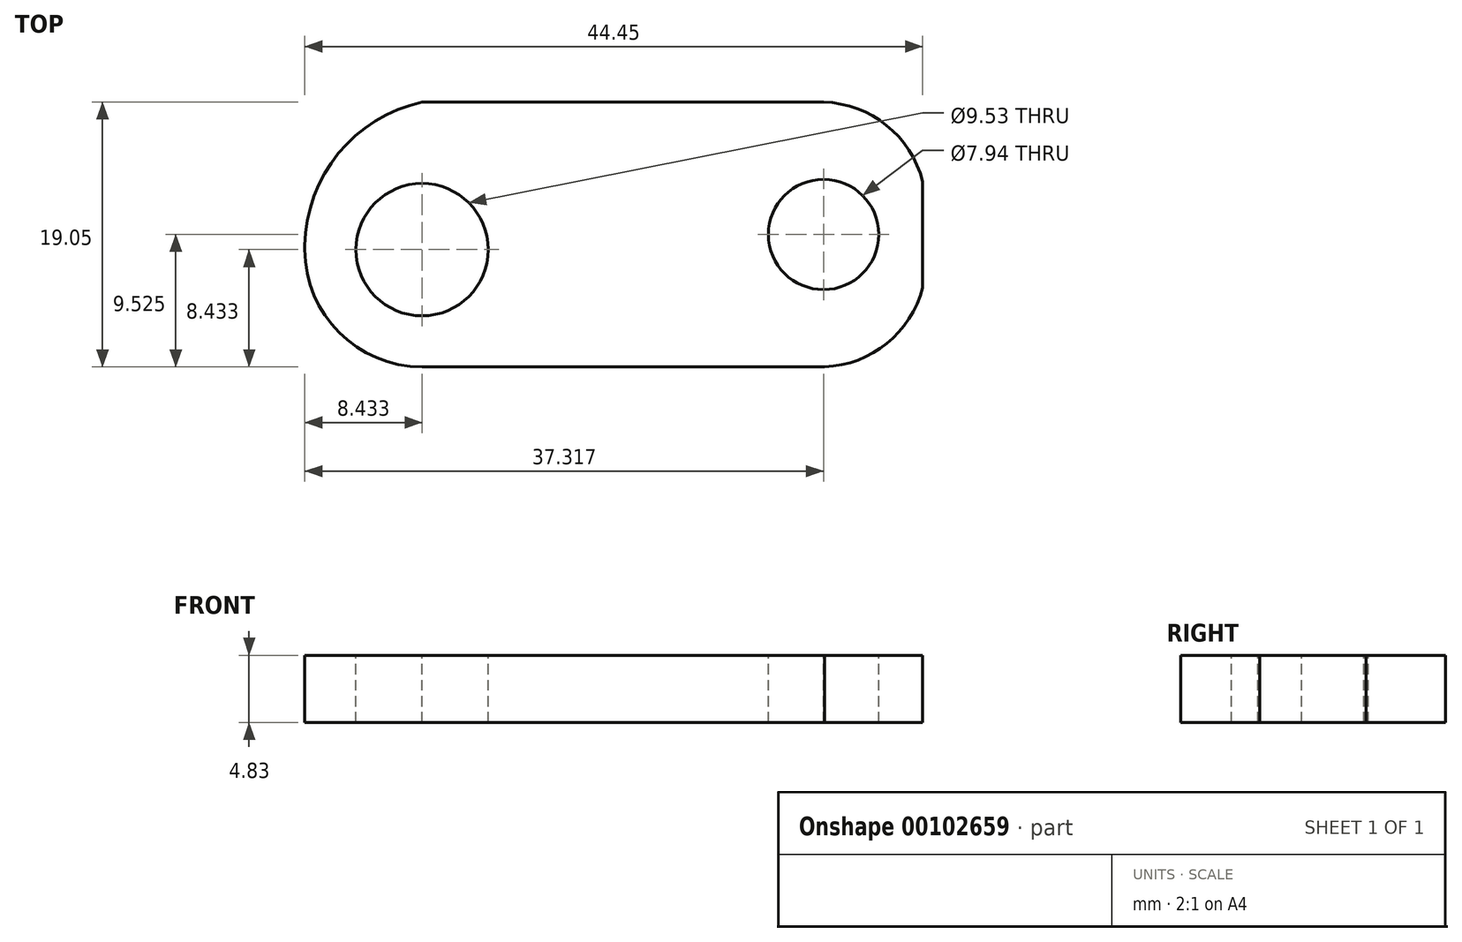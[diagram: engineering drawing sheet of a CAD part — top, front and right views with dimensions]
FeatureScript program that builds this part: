
annotation { "Feature Type Name" : "Feature", "Feature Type Description" : "" }
export const myFeature = defineFeature(function(context is Context, id is Id, definition is map)
    precondition{}
    {
        {
            var Q0;
            Q0=qCreatedBy(makeId("Top.planeOp"),FACE);
            var sketch = newSketch(context, id + "F0", { "sketchPlane" : qUnion([Q0])});
            skLineSegment(sketch, "E0.bottom", {"start": v(0, 0) * mm, "end": v(44.45, 0) * mm});
            skLineSegment(sketch, "E0.top", {"start": v(0, 19.05) * mm, "end": v(44.45, 19.05) * mm});
            skLineSegment(sketch, "E0.left", {"start": v(0, 0) * mm, "end": v(0, 19.05) * mm});
            skLineSegment(sketch, "E0.right", {"start": v(44.45, 0) * mm, "end": v(44.45, 19.05) * mm});
            skSolve(sketch);
        }
        {
            var Q0;
            Q0 = qSketchRegion(id + "F0", true);
            extrude(context, id + "F1", {"entities" : qUnion([Q0]), "depth" : 4.83 * mm});
        }
        {
            var Q0;
            Q0=makeQuery(id+"F1.opExtrude","CAP_FACE",FACE,{"disambiguationData":[OSD([sQuery(id+"F0.wireOp",EDGE,"E0.bottom"),sQuery(id+"F0.wireOp",EDGE,"E0.top"),sQuery(id+"F0.wireOp",EDGE,"E0.left"),sQuery(id+"F0.wireOp",EDGE,"E0.right")])],"isStart":false});
            var sketch = newSketch(context, id + "F2", { "sketchPlane" : qUnion([Q0])});
            skCircle(sketch, "E1", {"center": v(8.43, 8.43) * mm, "radius": 4.76 * mm});
            skCircle(sketch, "E2", {"center": v(37.32, 9.52) * mm, "radius": 3.97 * mm});
            skPoint(sketch, "E2.centerSnap0", {"position": v(44.45, 9.53) * mm});
            skArc(sketch, "E3", {"start": v(44.45, 13.34) * mm, "mid": v(41.83, 17.38) * mm, "end": v(37.32, 19.05) * mm});
            skArc(sketch, "E4", {"start": v(37.4, 0) * mm, "mid": v(41.86, 1.69) * mm, "end": v(44.45, 5.7) * mm});
            skLineSegment(sketch, "E5.0", {"start": v(44.45, 5.7) * mm, "end": v(44.45, 13.34) * mm});
            skPoint(sketch, "E6.orphan", {"position": v(44.45, 0) * mm});
            skPoint(sketch, "E7.orphan", {"position": v(44.45, 19.05) * mm});
            skArc(sketch, "E8", {"start": v(8.43, 19.05) * mm, "mid": v(2.32, 15.24) * mm, "end": v(0, 8.43) * mm});
            skLineSegment(sketch, "E9", {"start": v(0, 8.43) * mm, "end": v(0, 8.43) * mm});
            skArc(sketch, "E10", {"start": v(0, 8.43) * mm, "mid": v(2.55, 2.4) * mm, "end": v(8.66, 0) * mm});
            skSolve(sketch);
        }
        {
            var Q0;
            Q0 = qSketchRegion(id + "F2", true);
            var Q1;
            {var subQ0=sQuery(id+"F2.wireOp",EDGE,"E8");var subQ1=makeQuery(id+"F1.opExtrude","CAP_EDGE",EDGE,{"disambiguationData":[OSD([sQuery(id+"F0.wireOp",EDGE,"E0.top")])],"isStart":false});var subQ2=makeQuery(id+"F2.imprint","INTERSECT",VERTEX,{"derivedFrom":[subQ1,subQ0]});Q1=makeQuery(id+"F2.imprint","IMPRINT",FACE,{"disambiguationData":[TD([[makeQuery(id+"F2.imprint","IMPRINT",EDGE,{"disambiguationData":[TD([[subQ2,-1.0]])],"derivedFrom":subQ0}),-1.0]])]});}
            var Q2;
            {var subQ1=makeQuery(id+"F1.opExtrude","CAP_EDGE",EDGE,{"disambiguationData":[OSD([sQuery(id+"F0.wireOp",EDGE,"E0.left")])],"isStart":false});var subQ3=makeQuery(id+"F1.opExtrude","CAP_EDGE",EDGE,{"disambiguationData":[OSD([sQuery(id+"F0.wireOp",EDGE,"E0.bottom")])],"isStart":false});var subQ5=makeQuery(id+"F2.imprint","INTERSECT",VERTEX,{"derivedFrom":[subQ3,subQ1]});Q2=makeQuery(id+"F2.imprint","IMPRINT",FACE,{"disambiguationData":[TD([[makeQuery(id+"F2.imprint","IMPRINT",EDGE,{"disambiguationData":[TD([[subQ5,-1.0]])],"derivedFrom":subQ3}),1.0]])]});}
            var Q3;
            {var subQ0=sQuery(id+"F2.wireOp",EDGE,"E4");Q3=makeQuery(id+"F2.imprint","IMPRINT",FACE,{"disambiguationData":[TD([[makeQuery(id+"F2.imprint","IMPRINT",EDGE,{"derivedFrom":subQ0}),-1.0]])]});}
            var Q4;
            {var subQ0=sQuery(id+"F2.wireOp",EDGE,"E3");Q4=makeQuery(id+"F2.imprint","IMPRINT",FACE,{"disambiguationData":[TD([[makeQuery(id+"F2.imprint","IMPRINT",EDGE,{"derivedFrom":subQ0}),-1.0]])]});}
            extrude(context, id + "F3", {"entities" : qUnion([Q0, Q1, Q2, Q3, Q4]), "operationType" : NewBodyOperationType.REMOVE, "endBound" : BoundingType.THROUGH_ALL, "oppositeDirection" : true, "depth" : 25.4 * mm});
        }
    });
